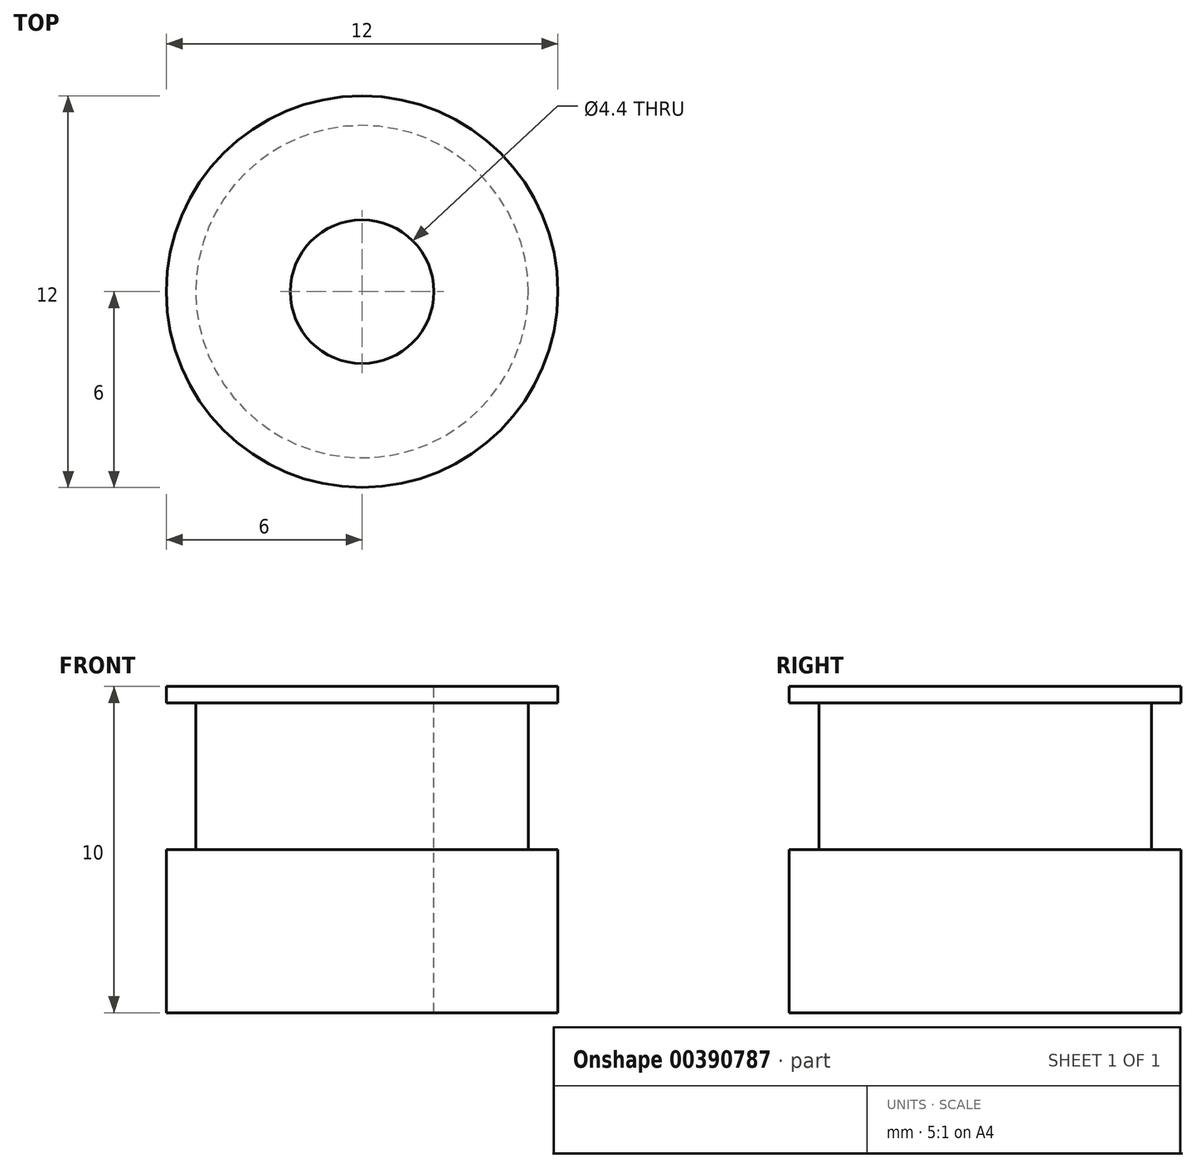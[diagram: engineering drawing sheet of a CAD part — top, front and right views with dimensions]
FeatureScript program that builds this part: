
annotation { "Feature Type Name" : "Feature", "Feature Type Description" : "" }
export const myFeature = defineFeature(function(context is Context, id is Id, definition is map)
    precondition{}
    {
        {
            var Q0;
            Q0=qCreatedBy(makeId("Top.planeOp"),FACE);
            var sketch = newSketch(context, id + "F0", { "sketchPlane" : qUnion([Q0]), "asVersion" : FeatureScriptVersionNumber.V593_MASTER_MODEL_DOC});
            skCircle(sketch, "E0", {"center": v(0, 0) * mm, "radius": 6 * mm});
            skCircle(sketch, "E1", {"center": v(0, 0) * mm, "radius": 5.1 * mm});
            skSolve(sketch);
        }
        {
            var Q0;
            Q0=makeQuery(id+"F0.imprint","IMPRINT",FACE,{"disambiguationData":[TD([[makeQuery(id+"F0.imprint","IMPRINT",EDGE,{"derivedFrom":sQuery(id+"F0.wireOp",EDGE,"E0")}),1.0]])]});
            var Q1;
            Q1=makeQuery(id+"F0.imprint","IMPRINT",FACE,{"disambiguationData":[TD([[makeQuery(id+"F0.imprint","IMPRINT",EDGE,{"derivedFrom":sQuery(id+"F0.wireOp",EDGE,"E1")}),1.0]])]});
            extrude(context, id + "F1", {"entities" : qUnion([Q0, Q1]), "depth" : 5 * mm, "offsetDistance" : 25 * mm});
        }
        {
            var Q0;
            Q0=makeQuery(id+"F0.imprint","IMPRINT",FACE,{"disambiguationData":[TD([[makeQuery(id+"F0.imprint","IMPRINT",EDGE,{"derivedFrom":sQuery(id+"F0.wireOp",EDGE,"E1")}),1.0]])]});
            extrude(context, id + "F2", {"entities" : qUnion([Q0]), "operationType" : NewBodyOperationType.ADD, "depth" : 10 * mm, "offsetDistance" : 25 * mm});
        }
        {
            var Q0;
            Q0=makeQuery(id+"F2.opExtrude","CAP_FACE",FACE,{"disambiguationData":[OSD([sQuery(id+"F0.wireOp",EDGE,"E1")])],"isStart":false});
            var sketch = newSketch(context, id + "F3", { "sketchPlane" : qUnion([Q0]), "asVersion" : FeatureScriptVersionNumber.V593_MASTER_MODEL_DOC});
            skCircle(sketch, "E2.0", {"center": v(0, 0) * mm, "radius": 6 * mm});
            skSolve(sketch);
        }
        {
            var Q0;
            Q0=makeQuery(id+"F3.imprint","IMPRINT",FACE,{"disambiguationData":[TD([[makeQuery(id+"F3.imprint","IMPRINT",EDGE,{"derivedFrom":sQuery(id+"F3.wireOp",EDGE,"E2.0")}),1.0]])]});
            var Q1;
            Q1=makeQuery(id+"F3.imprint","IMPRINT",FACE,{"disambiguationData":[TD([[makeQuery(id+"F3.imprint","IMPRINT",EDGE,{"derivedFrom":makeQuery(id+"F2.opExtrude","CAP_EDGE",EDGE,{"disambiguationData":[OSD([sQuery(id+"F0.wireOp",EDGE,"E1")])],"isStart":false})}),1.0]])]});
            extrude(context, id + "F4", {"entities" : qUnion([Q0, Q1]), "operationType" : NewBodyOperationType.ADD, "oppositeDirection" : true, "depth" : 0.5 * mm, "offsetDistance" : 25 * mm});
        }
        {
            var Q0;
            Q0=sQuery(id+"F0.wireOp",VERTEX,"E0.center");
            var Q1;
            Q1=makeQuery(id+"F1.opExtrude","SWEPT_BODY",BODY,{"disambiguationData":[OSD([sQuery(id+"F0.wireOp",EDGE,"E0")])]});
            hole(context, id + "F5", {"style" : HoleStyle.SIMPLE, "endStyle" : HoleEndStyle.THROUGH, "oppositeDirection" : true, "standardTappedOrClearance" : lookupTablePath({ "standard" : "ISO", "fit" : "Normal", "size" : "M4", "type" : "Clearance" }), "standardBlindInLast" : lookupTablePath({ "fit" : "Standard", "standard" : "ISO", "size" : "M4", "type" : "Clearance" }), "holeDiameter" : 4.4 * mm, "majorDiameter" : 5 * mm, "isTappedThrough" : true, "tappedDepth" : 3 * mm, "tapClearance" : 3, "locations" : qUnion([Q0]), "scope" : qUnion([Q1])});
        }
    });
